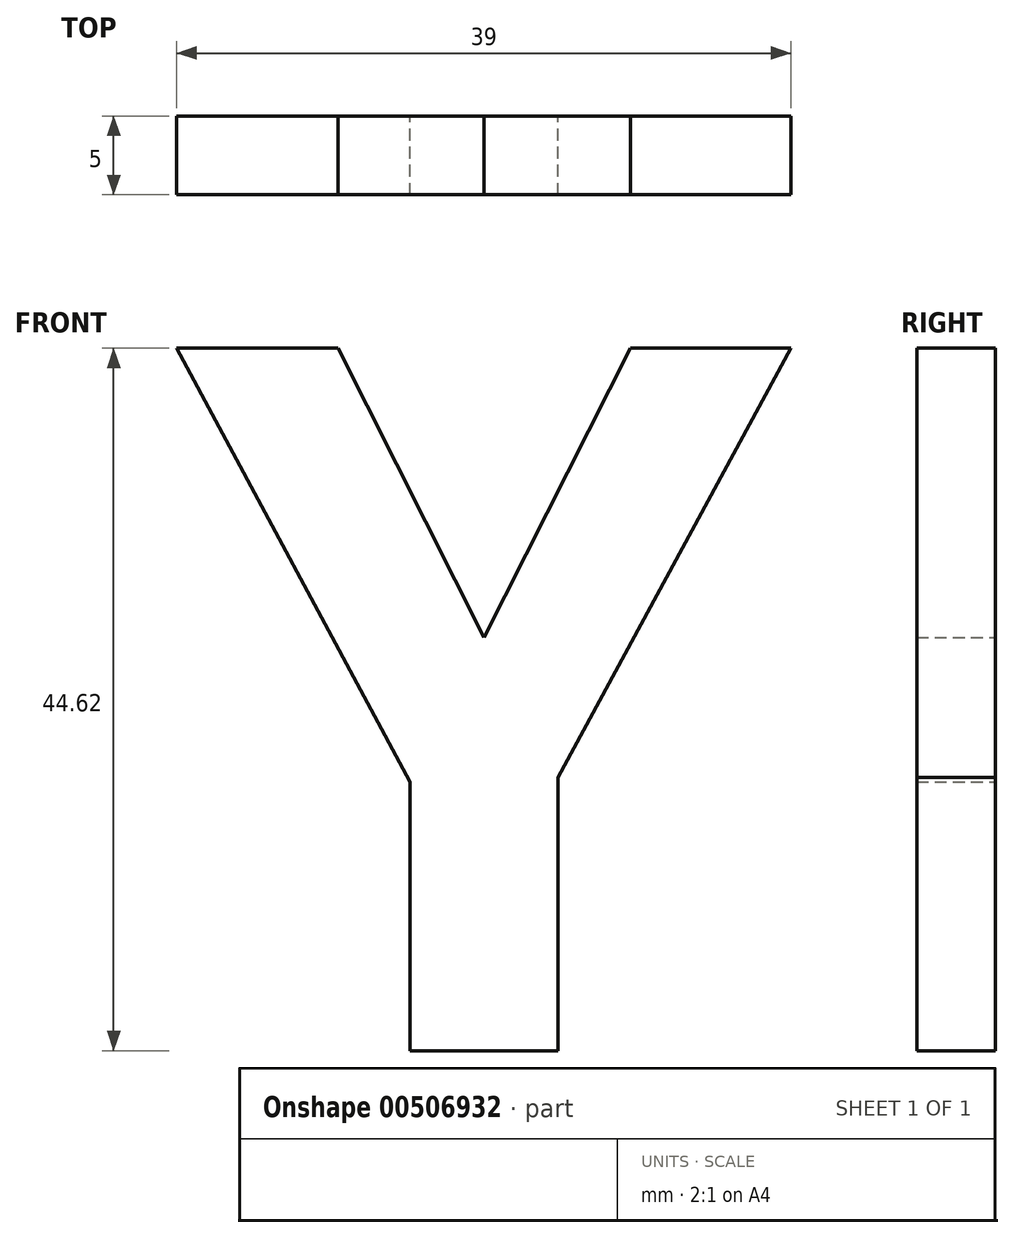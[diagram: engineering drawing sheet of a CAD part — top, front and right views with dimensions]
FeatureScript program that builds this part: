
annotation { "Feature Type Name" : "Feature", "Feature Type Description" : "" }
export const myFeature = defineFeature(function(context is Context, id is Id, definition is map)
    precondition{}
    {
        {
            var Q0;
            Q0=qCreatedBy(makeId("Front.planeOp"),FACE);
            var sketch = newSketch(context, id + "F0", { "sketchPlane" : qUnion([Q0])});
            skText(sketch, "E0", { "text": "Y", "fontName": "OpenSans-Bold.ttf"});
            const initialGuessF0  = {"E0": [-0.07223, 0.0257, 1, 0, 0.045]};
            skSetInitialGuess(sketch, initialGuessF0);
            skSolve(sketch);
        }
        {
            var Q0;
            Q0=makeQuery(id+"F0.imprint","IMPRINT",FACE,{"disambiguationData":[TD([[makeQuery(id+"F0.imprint","IMPRINT",EDGE,{"derivedFrom":sQuery(id+"F0.wireOp",EDGE,"E0.sketch_text.stroke-0")}),-1.0]])]});
            extrude(context, id + "F1", {"entities" : qUnion([Q0]), "depth" : 5 * mm});
        }
    });
